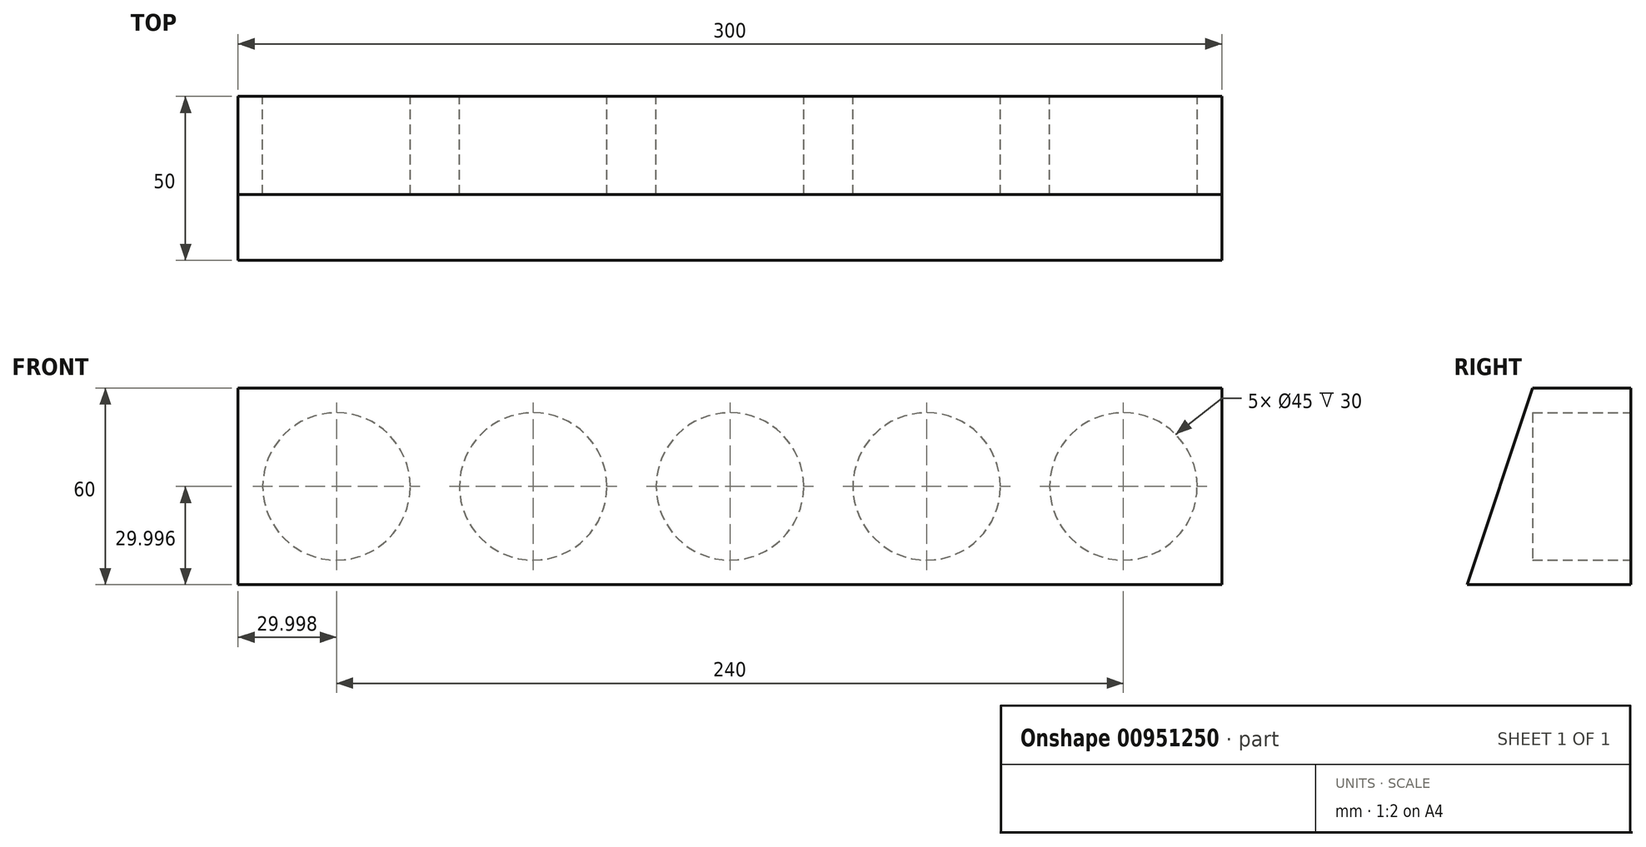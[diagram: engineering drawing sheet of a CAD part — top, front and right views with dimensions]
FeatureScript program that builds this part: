
annotation { "Feature Type Name" : "Feature", "Feature Type Description" : "" }
export const myFeature = defineFeature(function(context is Context, id is Id, definition is map)
    precondition{}
    {
        {
            var Q0;
            Q0=qCreatedBy(makeId("Front.planeOp"),FACE);
            var sketch = newSketch(context, id + "F0", { "sketchPlane" : qUnion([Q0])});
            skLineSegment(sketch, "E0.bottom", {"start": v(-242.24, 36.64) * mm, "end": v(57.76, 36.64) * mm});
            skLineSegment(sketch, "E0.top", {"start": v(-242.24, -23.36) * mm, "end": v(57.76, -23.36) * mm});
            skLineSegment(sketch, "E0.left", {"start": v(-242.24, 36.64) * mm, "end": v(-242.24, -23.36) * mm});
            skLineSegment(sketch, "E0.right", {"start": v(57.76, 36.64) * mm, "end": v(57.76, -23.36) * mm});
            skSolve(sketch);
        }
        {
            var Q0;
            Q0=makeQuery(id+"F0.imprint","IMPRINT",FACE,{"disambiguationData":[TD([[makeQuery(id+"F0.imprint","IMPRINT",EDGE,{"derivedFrom":sQuery(id+"F0.wireOp",EDGE,"E0.bottom")}),-1.0]])]});
            extrude(context, id + "F1", {"entities" : qUnion([Q0]), "depth" : 30 * mm, "offsetDistance" : 25 * mm});
        }
        {
            var Q0;
            Q0=makeQuery(id+"F1.opExtrude","SWEPT_FACE",FACE,{"disambiguationData":[OSD([sQuery(id+"F0.wireOp",EDGE,"E0.left")])]});
            var sketch = newSketch(context, id + "F2", { "sketchPlane" : qUnion([Q0])});
            skLineSegment(sketch, "E1", {"start": v(30, -23.36) * mm, "end": v(50, -23.36) * mm});
            skLineSegment(sketch, "E2", {"start": v(50, -23.36) * mm, "end": v(30, 36.64) * mm});
            skSolve(sketch);
        }
        {
            var Q0;
            Q0=makeQuery(id+"F2.imprint","IMPRINT",FACE,{"disambiguationData":[TD([[makeQuery(id+"F2.imprint","IMPRINT",EDGE,{"derivedFrom":sQuery(id+"F2.wireOp",EDGE,"E1")}),1.0]])]});
            extrude(context, id + "F3", {"entities" : qUnion([Q0]), "operationType" : NewBodyOperationType.ADD, "depth" : -300 * mm, "offsetDistance" : 25 * mm});
        }
        {
            var Q0;
            Q0=makeQuery(id+"F1.opExtrude","CAP_FACE",FACE,{"disambiguationData":[OSD([sQuery(id+"F0.wireOp",EDGE,"E0.bottom"),sQuery(id+"F0.wireOp",EDGE,"E0.top"),sQuery(id+"F0.wireOp",EDGE,"E0.left"),sQuery(id+"F0.wireOp",EDGE,"E0.right")])],"isStart":true});
            var sketch = newSketch(context, id + "F4", { "sketchPlane" : qUnion([Q0])});
            skLineSegment(sketch, "E3.bottom", {"start": v(-57.76, 36.64) * mm, "end": v(-27.76, 36.64) * mm});
            skLineSegment(sketch, "E3.left", {"start": v(-57.76, 36.64) * mm, "end": v(-57.76, 6.64) * mm});
            skLineSegment(sketch, "E4.bottom", {"start": v(-27.76, 36.64) * mm, "end": v(32.24, 36.64) * mm});
            skLineSegment(sketch, "E4.right", {"start": v(32.24, 36.64) * mm, "end": v(32.24, 6.64) * mm});
            skLineSegment(sketch, "E5.bottom", {"start": v(32.24, 36.64) * mm, "end": v(92.24, 36.64) * mm});
            skLineSegment(sketch, "E6.bottom", {"start": v(92.24, 36.64) * mm, "end": v(152.24, 36.64) * mm});
            skLineSegment(sketch, "E6.left", {"start": v(92.24, 36.64) * mm, "end": v(92.24, 6.64) * mm});
            skLineSegment(sketch, "E6.right", {"start": v(152.24, 36.64) * mm, "end": v(152.24, 6.64) * mm});
            skLineSegment(sketch, "E7.bottom", {"start": v(152.24, 36.64) * mm, "end": v(212.24, 36.64) * mm});
            skCircle(sketch, "E8", {"center": v(-27.76, 6.64) * mm, "radius": 22.5 * mm});
            skCircle(sketch, "E9", {"center": v(32.24, 6.64) * mm, "radius": 22.5 * mm});
            skCircle(sketch, "E10", {"center": v(92.24, 6.64) * mm, "radius": 22.5 * mm});
            skCircle(sketch, "E11", {"center": v(152.24, 6.64) * mm, "radius": 22.5 * mm});
            skCircle(sketch, "E12", {"center": v(212.24, 6.64) * mm, "radius": 22.5 * mm});
            skSolve(sketch);
        }
        {
            var Q0;
            Q0=makeQuery(id+"F4.imprint","IMPRINT",FACE,{"disambiguationData":[TD([[makeQuery(id+"F4.imprint","IMPRINT",EDGE,{"derivedFrom":sQuery(id+"F4.wireOp",EDGE,"E8")}),1.0]])]});
            var Q1;
            Q1=makeQuery(id+"F4.imprint","IMPRINT",FACE,{"disambiguationData":[TD([[makeQuery(id+"F4.imprint","IMPRINT",EDGE,{"derivedFrom":sQuery(id+"F4.wireOp",EDGE,"E9")}),1.0]])]});
            var Q2;
            Q2=makeQuery(id+"F4.imprint","IMPRINT",FACE,{"disambiguationData":[TD([[makeQuery(id+"F4.imprint","IMPRINT",EDGE,{"derivedFrom":sQuery(id+"F4.wireOp",EDGE,"E10")}),1.0]])]});
            var Q3;
            Q3=makeQuery(id+"F4.imprint","IMPRINT",FACE,{"disambiguationData":[TD([[makeQuery(id+"F4.imprint","IMPRINT",EDGE,{"derivedFrom":sQuery(id+"F4.wireOp",EDGE,"E11")}),1.0]])]});
            var Q4;
            Q4=makeQuery(id+"F4.imprint","IMPRINT",FACE,{"disambiguationData":[TD([[makeQuery(id+"F4.imprint","IMPRINT",EDGE,{"derivedFrom":sQuery(id+"F4.wireOp",EDGE,"E12")}),1.0]])]});
            extrude(context, id + "F5", {"entities" : qUnion([Q0, Q1, Q2, Q3, Q4]), "operationType" : NewBodyOperationType.REMOVE, "oppositeDirection" : true, "depth" : 30 * mm, "offsetDistance" : 25 * mm});
        }
    });
